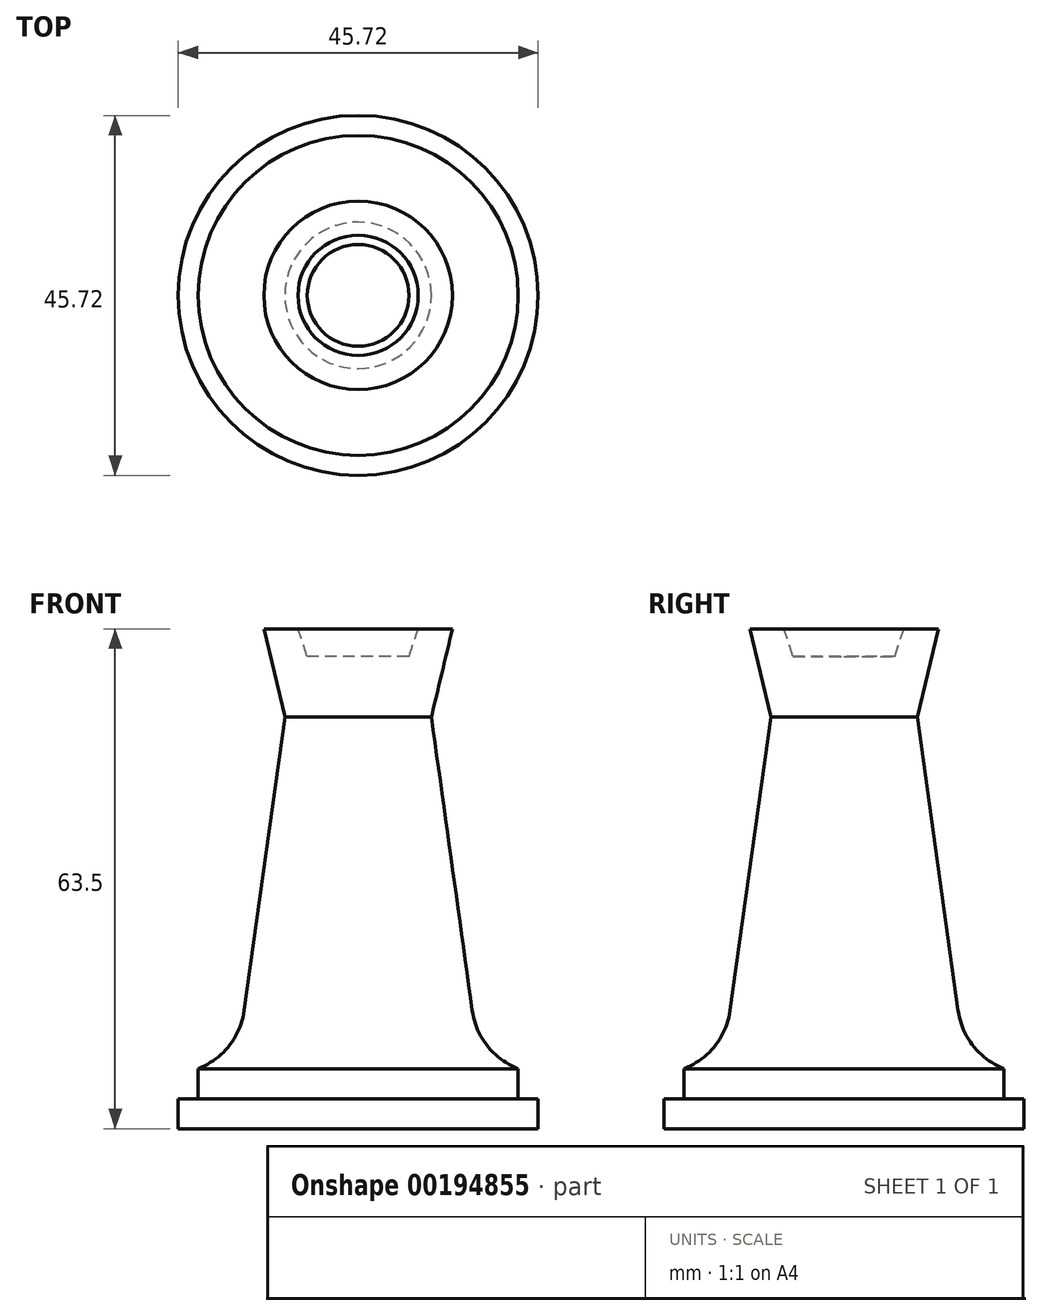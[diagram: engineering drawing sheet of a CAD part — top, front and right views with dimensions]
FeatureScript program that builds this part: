
annotation { "Feature Type Name" : "Feature", "Feature Type Description" : "" }
export const myFeature = defineFeature(function(context is Context, id is Id, definition is map)
    precondition{}
    {
        {
            var Q0;
            Q0=qCreatedBy(makeId("Front.planeOp"),FACE);
            var sketch = newSketch(context, id + "F0", { "sketchPlane" : qUnion([Q0])});
            skLineSegment(sketch, "E0", {"start": v(0, 42.55) * mm, "end": v(0, -20.95) * mm});
            skLineSegment(sketch, "E1", {"start": v(0, -20.95) * mm, "end": v(22.86, -20.95) * mm});
            skLineSegment(sketch, "E2", {"start": v(22.86, -20.95) * mm, "end": v(22.86, -17.14) * mm});
            skLineSegment(sketch, "E3", {"start": v(22.86, -17.14) * mm, "end": v(20.32, -17.14) * mm});
            skLineSegment(sketch, "E4", {"start": v(20.32, -17.14) * mm, "end": v(20.32, -13.33) * mm});
            skLineSegment(sketch, "E5", {"start": v(0, -13.35) * mm, "end": v(0, -9.48) * mm});
            skLineSegment(sketch, "E6", {"start": v(11.98, 42.55) * mm, "end": v(7.63, 42.55) * mm});
            skLineSegment(sketch, "E7", {"start": v(7.63, 42.55) * mm, "end": v(6.46, 39.04) * mm});
            skLineSegment(sketch, "E8", {"start": v(6.46, 39.04) * mm, "end": v(0, 39.04) * mm});
            skPoint(sketch, "E9.endSnap0", {"position": v(4, -9.48) * mm});
            skLineSegment(sketch, "E10", {"start": v(11.98, 42.55) * mm, "end": v(9.3, 31.35) * mm});
            skLineSegment(sketch, "E11", {"start": v(9.3, 31.35) * mm, "end": v(14.5, -5.95) * mm});
            skArc(sketch, "E12", {"start": v(14.5, -5.95) * mm, "mid": v(16.4, -10.43) * mm, "end": v(20.32, -13.33) * mm});
            skSolve(sketch);
        }
        {
            var Q0;
            {var subQ3=sQuery(id+"F0.wireOp",EDGE,"E1");Q0=makeQuery(id+"F0.imprint","IMPRINT",FACE,{"disambiguationData":[TD([[makeQuery(id+"F0.imprint","IMPRINT",EDGE,{"derivedFrom":subQ3}),1.0]])]});}
            var Q1;
            Q1=sQuery(id+"F0.wireOp",EDGE,"E0");
            revolve(context, id + "F1", {"entities" : qUnion([Q0]), "axis" : qUnion([Q1]), "revolveType" : RevolveType.FULL});
        }
    });
